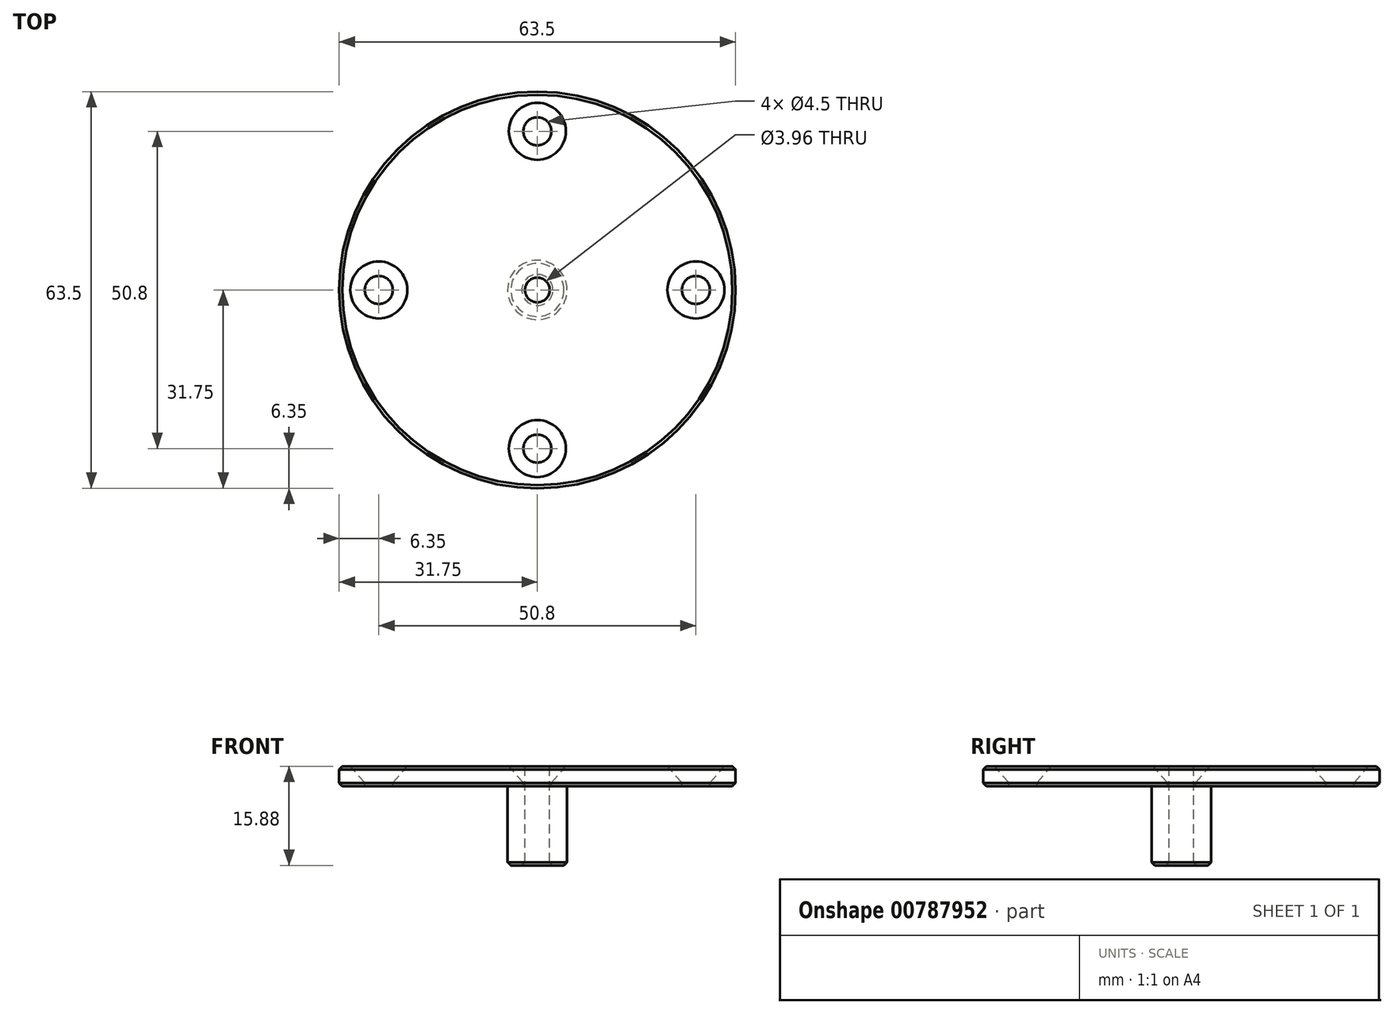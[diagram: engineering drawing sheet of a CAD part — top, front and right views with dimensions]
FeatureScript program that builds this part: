
annotation { "Feature Type Name" : "Feature", "Feature Type Description" : "" }
export const myFeature = defineFeature(function(context is Context, id is Id, definition is map)
    precondition{}
    {
        {
            var Q0;
            Q0=qCreatedBy(makeId("Top.planeOp"),FACE);
            var sketch = newSketch(context, id + "F0", { "sketchPlane" : qUnion([Q0])});
            skCircle(sketch, "E0", {"center": v(0, 0) * mm, "radius": 31.75 * mm});
            skSolve(sketch);
        }
        {
            var Q0;
            Q0 = qSketchRegion(id + "F0", true);
            extrude(context, id + "F1", {"entities" : qUnion([Q0]), "depth" : 3.17 * mm, "offsetDistance" : 25.4 * mm});
        }
        {
            var Q0;
            Q0=makeQuery(id+"F1.opExtrude","CAP_FACE",FACE,{"disambiguationData":[OSD([sQuery(id+"F0.wireOp",EDGE,"E0")])],"isStart":true});
            var sketch = newSketch(context, id + "F2", { "sketchPlane" : qUnion([Q0])});
            skCircle(sketch, "E1", {"center": v(0, 0) * mm, "radius": 4.76 * mm});
            skSolve(sketch);
        }
        {
            var Q0;
            Q0 = qSketchRegion(id + "F2", true);
            extrude(context, id + "F3", {"entities" : qUnion([Q0]), "operationType" : NewBodyOperationType.ADD, "depth" : 12.7 * mm, "offsetDistance" : 25.4 * mm});
        }
        {
            var Q0;
            Q0=makeQuery(id+"F1.opExtrude","CAP_FACE",FACE,{"disambiguationData":[OSD([sQuery(id+"F0.wireOp",EDGE,"E0")])],"isStart":false});
            var sketch = newSketch(context, id + "F4", { "sketchPlane" : qUnion([Q0])});
            skPoint(sketch, "E2", {"position": v(0, 25.4) * mm});
            skPoint(sketch, "E3", {"position": v(25.4, 0) * mm});
            skPoint(sketch, "E4", {"position": v(0, -25.4) * mm});
            skPoint(sketch, "E5", {"position": v(-25.4, 0) * mm});
            skSolve(sketch);
        }
        {
            var Q0;
            Q0=sQuery(id+"F4.wireOp",VERTEX,"E5");
            var Q1;
            Q1=sQuery(id+"F4.wireOp",VERTEX,"E2");
            var Q2;
            Q2=sQuery(id+"F4.wireOp",VERTEX,"E3");
            var Q3;
            Q3=sQuery(id+"F4.wireOp",VERTEX,"E4");
            var Q4;
            Q4=makeQuery(id+"F1.opExtrude","SWEPT_BODY",BODY,{"disambiguationData":[OSD([sQuery(id+"F0.wireOp",EDGE,"E0")])]});
            hole(context, id + "F5", {"style" : HoleStyle.C_SINK, "endStyle" : HoleEndStyle.THROUGH, "standardTappedOrClearance" : lookupTablePath({ "fit" : "Free", "standard" : "ANSI", "size" : "#8", "type" : "Clearance" }), "standardBlindInLast" : lookupTablePath({ "fit" : "Free", "standard" : "ANSI", "engagement" : "75%", "pitch" : "32 tpi", "size" : "#8", "type" : "Clearance & tapped" }), "holeDiameter" : 4.5 * mm, "cSinkDiameter" : 9.12 * mm, "cSinkAngle" : 82 * degree, "majorDiameter" : 4.17 * mm, "tappedDepth" : 9.52 * mm, "tapClearance" : 3, "startFromSketch" : true, "locations" : qUnion([Q0, Q1, Q2, Q3]), "scope" : qUnion([Q4])});
        }
        {
            var Q0;
            Q0=makeQuery(id+"F1.opExtrude","CAP_FACE",FACE,{"disambiguationData":[OSD([sQuery(id+"F0.wireOp",EDGE,"E0")])],"isStart":false});
            var sketch = newSketch(context, id + "F6", { "sketchPlane" : qUnion([Q0])});
            skCircle(sketch, "E6", {"center": v(0, 0) * mm, "radius": 1.98 * mm});
            skSolve(sketch);
        }
        {
            var Q0;
            Q0 = qSketchRegion(id + "F6", true);
            extrude(context, id + "F7", {"entities" : qUnion([Q0]), "operationType" : NewBodyOperationType.REMOVE, "endBound" : BoundingType.THROUGH_ALL, "oppositeDirection" : true, "depth" : 25.4 * mm, "offsetDistance" : 25.4 * mm});
        }
        {
            var Q0;
            Q0=makeQuery(id+"F1.opExtrude","CAP_EDGE",EDGE,{"disambiguationData":[OSD([sQuery(id+"F0.wireOp",EDGE,"E0")])],"isStart":false});
            var Q1;
            Q1=makeQuery(id+"F7.boolean.opBoolean","COPY",EDGE,{"derivedFrom":makeQuery(id+"F7.opExtrude","CAP_EDGE",EDGE,{"disambiguationData":[OSD([sQuery(id+"F6.wireOp",EDGE,"E6")])],"isStart":true})});
            var Q2;
            Q2=makeQuery(id+"F1.opExtrude","CAP_EDGE",EDGE,{"disambiguationData":[OSD([sQuery(id+"F0.wireOp",EDGE,"E0")])],"isStart":true});
            var Q3;
            Q3=makeQuery(id+"F3.opExtrude","CAP_EDGE",EDGE,{"disambiguationData":[OSD([sQuery(id+"F2.wireOp",EDGE,"E1")])],"isStart":false});
            var Q4;
            Q4=makeQuery(id+"F7.boolean.opBoolean","INTERSECT",EDGE,{"derivedFrom":[makeQuery(id+"F3.opExtrude","CAP_FACE",FACE,{"disambiguationData":[OSD([sQuery(id+"F2.wireOp",EDGE,"E1")])],"isStart":false}),makeQuery(id+"F7.opExtrude","SWEPT_FACE",FACE,{"disambiguationData":[OSD([sQuery(id+"F6.wireOp",EDGE,"E6")])]})]});
            var Q5;
            Q5=makeQuery(id+"F3.opExtrude","CAP_EDGE",EDGE,{"disambiguationData":[OSD([sQuery(id+"F2.wireOp",EDGE,"E1")])],"isStart":true});
            chamfer(context, id + "F8", {"entities" : qUnion([Q0, Q1, Q2, Q3, Q4, Q5]), "width" : 0.5 * mm, "tangentPropagation" : true});
        }
    });
